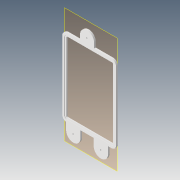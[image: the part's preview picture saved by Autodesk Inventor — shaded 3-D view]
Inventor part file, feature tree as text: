
AUTODESK INVENTOR PART (.ipt)
format: ipt  version: 2022 (Build 260153000, 153)  size: 155,136 bytes
history: native  units: mm
features: other x6, reference x5, extrude x2, sketch x2, plane x1
ambient origin geometry x8: Origin, YZ Plane, XZ Plane, XY Plane, X Axis, Y Axis, Z Axis, Center Point
bodies: Volumenkörper1 (feature_tree)
feature tree (16):
  plane  "Arbeitsebene1"
  extrude  "Extrusion1"  Depth=1.5mm
  extrude  "Extrusion2"  Depth=1.0mm
  sketch  "Skizze1"  dims[d0=5.0mm d1=1.5mm]
  reference  "Referenz1"
  reference  "Referenz2"
  reference  "Referenz3"
  reference  "Referenz4"
  sketch  "Skizze2"  dims[d2=25.0mm d3=2.8mm d4=2.8mm d5=2.8mm d6=3.0mm d7=0.0mm d8=1.0mm d9=1.0mm d10=0.0mm]
  reference  "Referenz5"
  other  "Omniscope_new_v0.iam"
  other  "00_24wellplate_base:1"
  other  "00_Z_Focus_CCTV_Camera:3"
  other  "00_Z_Focus_CCTV_Camera:2"
  other  "00_Z_Focus_CCTV_Camera:1"
  other  "Omniscope_lensmount_v0:1"
